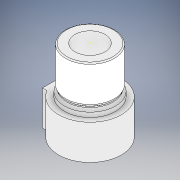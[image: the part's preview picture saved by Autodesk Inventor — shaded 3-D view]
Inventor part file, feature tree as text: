
AUTODESK INVENTOR PART (.ipt)
format: ipt  version: 2019 (Build 230136000, 136)  size: 174,592 bytes
history: native  units: mm
features: sketch x9, extrude x7, fillet x2, thread x2, chamfer x1
ambient origin geometry x8: Origin, YZ Plane, XZ Plane, XY Plane, X Axis, Y Axis, Z Axis, Center Point
bodies: Solid1 (feature_tree)
feature tree (21):
  extrude  "Extrusion1"  Depth=7.0mm
  extrude  "Extrusion2"  Depth=15.0mm TaperAngle=0.0deg
  extrude  "Extrusion3"  Depth=2.0mm TaperAngle=0.0deg
  extrude  "Extrusion4"  Depth=0.5mm TaperAngle=0.0deg
  fillet  "Fillet1"  Radius=21.0mm
  chamfer  "Chamfer1"  Distance=16.0mm
  fillet  "Fillet2"  Radius=1.0mm
  thread  "Thread1"  [1 undecoded]
  sketch  "Sketch5"  dims[d19=0.5mm d20=10.0mm d21=0.0mm]
  extrude  "Extrusion5"  Depth=10.0mm TaperAngle=0.0deg
  extrude  "Extrusion6"  Depth=25.0mm TaperAngle=0.0deg
  thread  "Thread2"  [1 undecoded]
  extrude  "Extrusion7"  Depth=10.0mm TaperAngle=0.0deg
  sketch  "Sketch9"  dims[d31=18.0mm d32=0.0mm]
  sketch  "Sketch1"  dims[d0=27.0mm d1=7.0mm]
  sketch  "Sketch2"  dims[d3=14.0mm d4=15.0mm d5=0.0mm]
  sketch  "Sketch3"  dims[d6=22.0mm d7=2.0mm d8=0.0mm]
  sketch  "Sketch4"  dims[d9=20.0mm d10=2.0mm d11=0.0mm d12=21.0mm d13=16.0mm d14=0.0mm d15=1.0mm d16=0.5mm d17=2.0mm d18=45.0deg]
  sketch  "Sketch6"  dims[d22=15.0mm d23=25.0mm d24=0.0mm d25=9.0mm]
  sketch  "Sketch7"  dims[d26=18.0mm d27=0.0mm d28=10.0mm d29=0.0mm]
  sketch  "Sketch8"  dims[d30=13.0mm]
note: 2 required parameter values undecoded (feature->parameter linkage not recoverable at this tier; creation-order binding heuristic only, values carry confidence <= 0.55)
